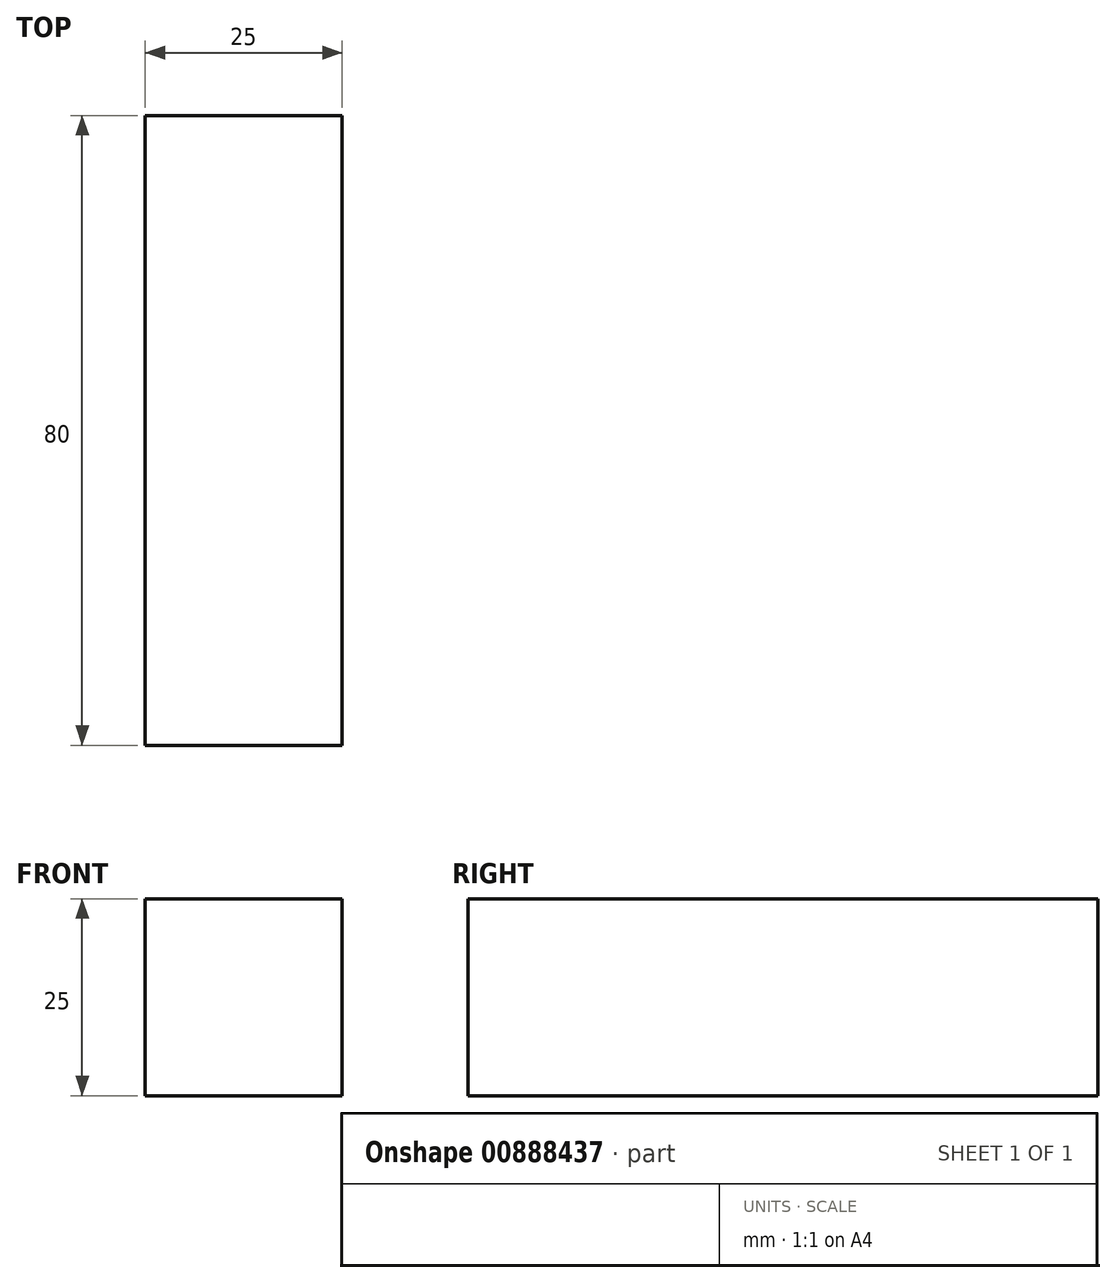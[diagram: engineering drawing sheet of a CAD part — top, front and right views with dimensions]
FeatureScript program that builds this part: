
annotation { "Feature Type Name" : "Feature", "Feature Type Description" : "" }
export const myFeature = defineFeature(function(context is Context, id is Id, definition is map)
    precondition{}
    {
        {
            var Q0;
            Q0=qCreatedBy(makeId("Top.planeOp"),FACE);
            var sketch = newSketch(context, id + "F0", { "sketchPlane" : qUnion([Q0])});
            skLineSegment(sketch, "E0.bottom", {"start": v(-12.5, 40) * mm, "end": v(12.5, 40) * mm});
            skLineSegment(sketch, "E0.top", {"start": v(-12.5, -40) * mm, "end": v(12.5, -40) * mm});
            skLineSegment(sketch, "E0.left", {"start": v(-12.5, 40) * mm, "end": v(-12.5, -40) * mm});
            skLineSegment(sketch, "E0.right", {"start": v(12.5, 40) * mm, "end": v(12.5, -40) * mm});
            skPoint(sketch, "E0.middle", {"position": v(0, 0) * mm});
            skSolve(sketch);
        }
        {
            var Q0;
            Q0 = qSketchRegion(id + "F0", true);
            extrude(context, id + "F1", {"entities" : qUnion([Q0]), "depth" : 25 * mm, "offsetDistance" : 25 * mm});
        }
    });
